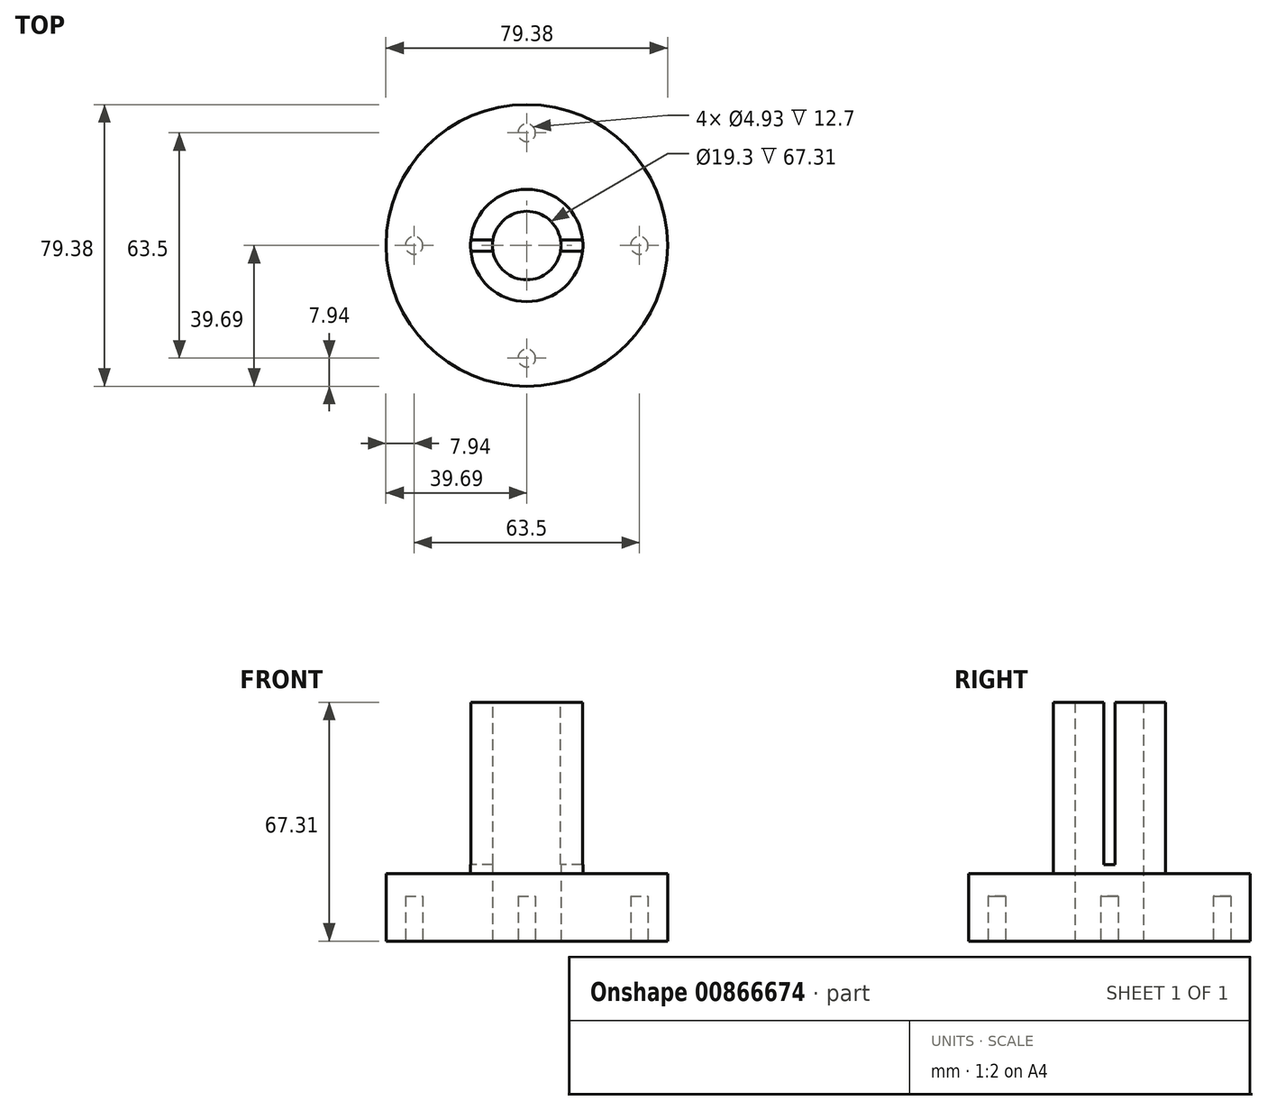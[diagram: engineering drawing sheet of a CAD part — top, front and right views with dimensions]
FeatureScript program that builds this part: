
annotation { "Feature Type Name" : "Feature", "Feature Type Description" : "" }
export const myFeature = defineFeature(function(context is Context, id is Id, definition is map)
    precondition{}
    {
        {
            var Q0;
            Q0=qCreatedBy(makeId("Top.planeOp"),FACE);
            var sketch = newSketch(context, id + "F0", { "sketchPlane" : qUnion([Q0])});
            skCircle(sketch, "E0", {"center": v(0, 0) * mm, "radius": 39.69 * mm});
            skCircle(sketch, "E1", {"center": v(0, 0) * mm, "radius": 9.65 * mm});
            skSolve(sketch);
        }
        {
            var Q0;
            Q0=makeQuery(id+"F0.imprint","IMPRINT",FACE,{"disambiguationData":[TD([[makeQuery(id+"F0.imprint","IMPRINT",EDGE,{"derivedFrom":sQuery(id+"F0.wireOp",EDGE,"E0")}),1.0]])]});
            extrude(context, id + "F1", {"entities" : qUnion([Q0]), "depth" : 19.05 * mm, "offsetDistance" : 25.4 * mm});
        }
        {
            var Q0;
            Q0=makeQuery(id+"F1.opExtrude","CAP_FACE",FACE,{"disambiguationData":[OSD([sQuery(id+"F0.wireOp",EDGE,"E0"),sQuery(id+"F0.wireOp",EDGE,"E1")])],"isStart":false});
            var sketch = newSketch(context, id + "F2", { "sketchPlane" : qUnion([Q0])});
            skCircle(sketch, "E2", {"center": v(0, 0) * mm, "radius": 15.84 * mm});
            skSolve(sketch);
        }
        {
            var Q0;
            Q0=makeQuery(id+"F2.imprint","IMPRINT",FACE,{"disambiguationData":[TD([[makeQuery(id+"F2.imprint","IMPRINT",EDGE,{"derivedFrom":sQuery(id+"F2.wireOp",EDGE,"E2")}),1.0]])]});
            extrude(context, id + "F3", {"entities" : qUnion([Q0]), "operationType" : NewBodyOperationType.ADD, "depth" : 48.26 * mm, "offsetDistance" : 25.4 * mm});
        }
        {
            var Q0;
            Q0=makeQuery(id+"F1.opExtrude","CAP_FACE",FACE,{"disambiguationData":[OSD([sQuery(id+"F0.wireOp",EDGE,"E0"),sQuery(id+"F0.wireOp",EDGE,"E1")])],"isStart":true});
            var sketch = newSketch(context, id + "F4", { "sketchPlane" : qUnion([Q0])});
            skCircle(sketch, "E3", {"center": v(-31.75, 0) * mm, "radius": 2.46 * mm});
            skCircle(sketch, "E4.1.0", {"center": v(0, -31.75) * mm, "radius": 2.46 * mm});
            skCircle(sketch, "E4.2.0", {"center": v(31.75, 0) * mm, "radius": 2.46 * mm});
            skCircle(sketch, "E4.3.0", {"center": v(0, 31.75) * mm, "radius": 2.46 * mm});
            skPoint(sketch, "E4.center", {"position": v(0, 0) * mm});
            skSolve(sketch);
        }
        {
            var Q0;
            Q0=makeQuery(id+"F4.imprint","IMPRINT",FACE,{"disambiguationData":[TD([[makeQuery(id+"F4.imprint","IMPRINT",EDGE,{"derivedFrom":sQuery(id+"F4.wireOp",EDGE,"E3")}),1.0]])]});
            var Q1;
            Q1=makeQuery(id+"F4.imprint","IMPRINT",FACE,{"disambiguationData":[TD([[makeQuery(id+"F4.imprint","IMPRINT",EDGE,{"derivedFrom":sQuery(id+"F4.wireOp",EDGE,"E4.1.0")}),1.0]])]});
            var Q2;
            Q2=makeQuery(id+"F4.imprint","IMPRINT",FACE,{"disambiguationData":[TD([[makeQuery(id+"F4.imprint","IMPRINT",EDGE,{"derivedFrom":sQuery(id+"F4.wireOp",EDGE,"E4.3.0")}),1.0]])]});
            var Q3;
            Q3=makeQuery(id+"F4.imprint","IMPRINT",FACE,{"disambiguationData":[TD([[makeQuery(id+"F4.imprint","IMPRINT",EDGE,{"derivedFrom":sQuery(id+"F4.wireOp",EDGE,"E4.2.0")}),1.0]])]});
            extrude(context, id + "F5", {"entities" : qUnion([Q0, Q1, Q2, Q3]), "operationType" : NewBodyOperationType.REMOVE, "oppositeDirection" : true, "depth" : 12.7 * mm, "offsetDistance" : 25.4 * mm});
        }
        {
            var Q0;
            Q0=makeQuery(id+"F3.opExtrude","CAP_FACE",FACE,{"disambiguationData":[OSD([sQuery(id+"F0.wireOp",EDGE,"E1"),sQuery(id+"F2.wireOp",EDGE,"E2")])],"isStart":false});
            var sketch = newSketch(context, id + "F6", { "sketchPlane" : qUnion([Q0])});
            skLineSegment(sketch, "E5.bottom", {"start": v(25.4, -1.59) * mm, "end": v(-25.4, -1.59) * mm});
            skLineSegment(sketch, "E5.top", {"start": v(25.4, 1.59) * mm, "end": v(-25.4, 1.59) * mm});
            skLineSegment(sketch, "E5.left", {"start": v(25.4, -1.59) * mm, "end": v(25.4, 1.59) * mm});
            skLineSegment(sketch, "E5.right", {"start": v(-25.4, -1.59) * mm, "end": v(-25.4, 1.59) * mm});
            skPoint(sketch, "E5.middle", {"position": v(0, 0) * mm});
            skSolve(sketch);
        }
        {
            var Q0;
            {var subQ0=sQuery(id+"F6.wireOp",EDGE,"E5.bottom");var subQ1=makeQuery(id+"F3.opExtrude","CAP_EDGE",EDGE,{"disambiguationData":[OSD([sQuery(id+"F2.wireOp",EDGE,"E2")])],"isStart":false});var subQ2=makeQuery(id+"F6.imprint","INTERSECT",VERTEX,{"disambiguationData":[OD(1.0)],"derivedFrom":[subQ1,subQ0]});Q0=makeQuery(id+"F6.imprint","IMPRINT",FACE,{"disambiguationData":[TD([[makeQuery(id+"F6.imprint","IMPRINT",EDGE,{"disambiguationData":[TD([[subQ2,1.0]])],"derivedFrom":subQ0}),-1.0]])]});}
            var Q1;
            {var subQ0=sQuery(id+"F6.wireOp",EDGE,"E5.bottom");var subQ1=makeQuery(id+"F3.opExtrude","CAP_EDGE",EDGE,{"disambiguationData":[OSD([sQuery(id+"F2.wireOp",EDGE,"E2")])],"isStart":false});var subQ2=makeQuery(id+"F6.imprint","INTERSECT",VERTEX,{"disambiguationData":[OD(0.0)],"derivedFrom":[subQ1,subQ0]});Q1=makeQuery(id+"F6.imprint","IMPRINT",FACE,{"disambiguationData":[TD([[makeQuery(id+"F6.imprint","IMPRINT",EDGE,{"disambiguationData":[TD([[subQ2,-1.0]])],"derivedFrom":subQ0}),-1.0]])]});}
            extrude(context, id + "F7", {"entities" : qUnion([Q0, Q1]), "operationType" : NewBodyOperationType.REMOVE, "oppositeDirection" : true, "depth" : 45.72 * mm, "offsetDistance" : 25.4 * mm});
        }
    });
